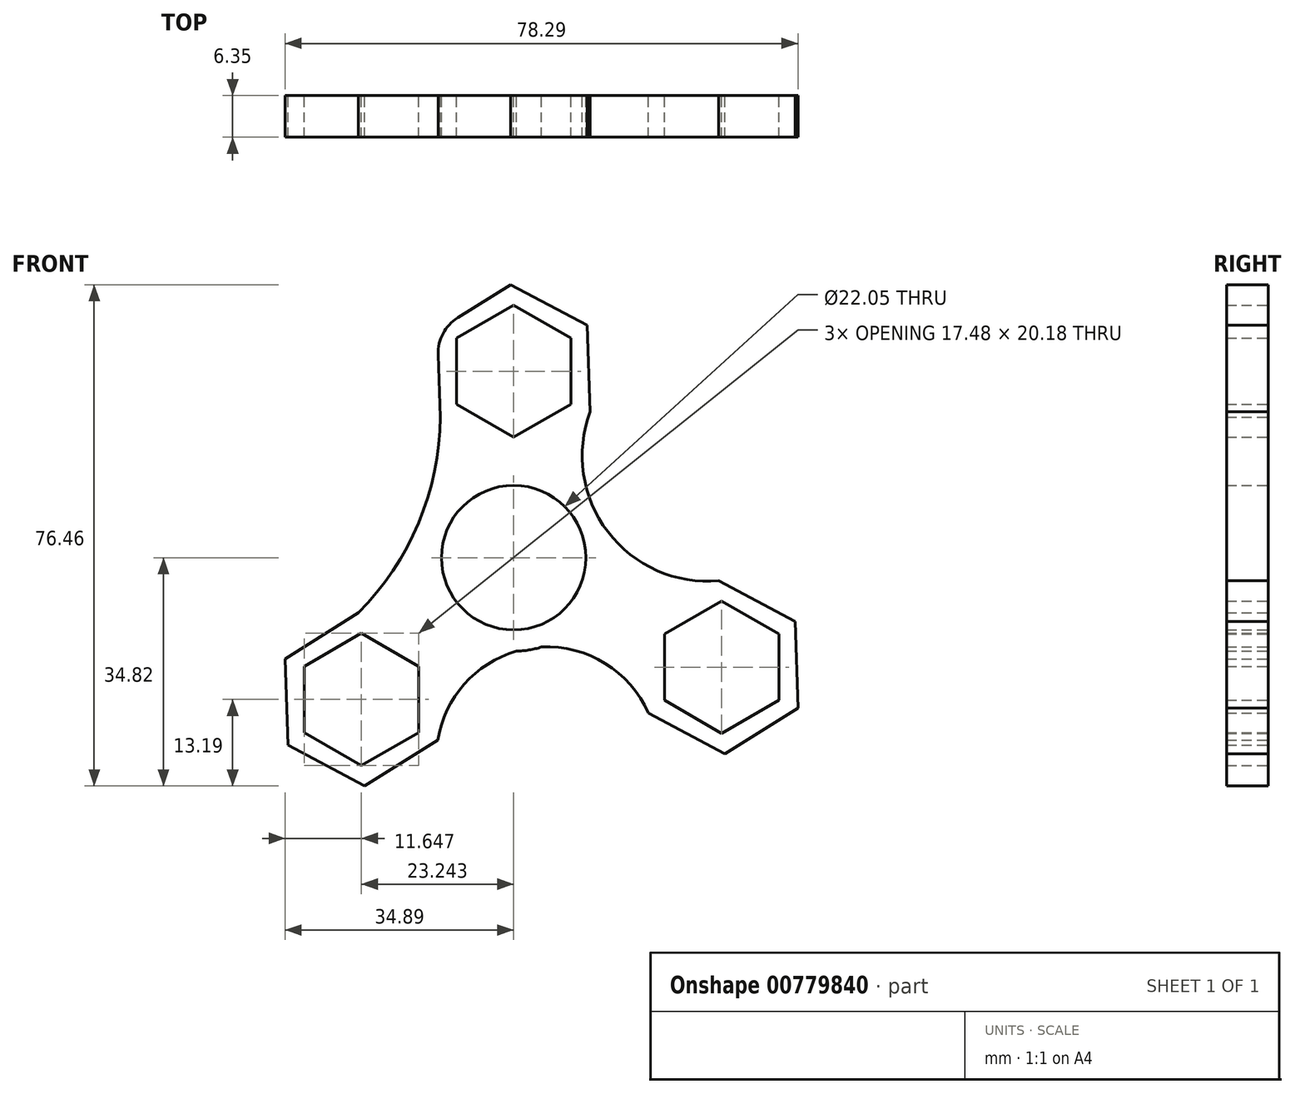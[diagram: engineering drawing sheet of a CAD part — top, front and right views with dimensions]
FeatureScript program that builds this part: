
annotation { "Feature Type Name" : "Feature", "Feature Type Description" : "" }
export const myFeature = defineFeature(function(context is Context, id is Id, definition is map)
    precondition{}
    {
        {
            var Q0;
            Q0=qCreatedBy(makeId("Front.planeOp"),FACE);
            var sketch = newSketch(context, id + "F0", { "sketchPlane" : qUnion([Q0])});
            skCircle(sketch, "E0", {"center": v(0, 0) * mm, "radius": 11.02 * mm});
            skCircle(sketch, "E1", {"center": v(0, 0) * mm, "radius": 14.29 * mm});
            skCircle(sketch, "E2.cCircle", {"center": v(0, 28.45) * mm, "radius": 8.74 * mm, "construction": true});
            skLineSegment(sketch, "E2.0", {"start": v(8.74, 33.5) * mm, "end": v(8.74, 23.4) * mm});
            skLineSegment(sketch, "E2.1", {"start": v(8.74, 23.4) * mm, "end": v(0, 18.36) * mm});
            skLineSegment(sketch, "E2.2", {"start": v(0, 18.36) * mm, "end": v(-8.74, 23.4) * mm});
            skLineSegment(sketch, "E2.3", {"start": v(-8.74, 23.4) * mm, "end": v(-8.74, 33.5) * mm});
            skLineSegment(sketch, "E2.4", {"start": v(-8.74, 33.5) * mm, "end": v(0, 38.54) * mm});
            skLineSegment(sketch, "E2.5", {"start": v(0, 38.54) * mm, "end": v(8.74, 33.5) * mm});
            skPoint(sketch, "E2.0.midPoint", {"position": v(8.74, 28.45) * mm});
            skCircle(sketch, "E3.cCircle", {"center": v(0, 28.45) * mm, "radius": 11.43 * mm, "construction": true});
            skLineSegment(sketch, "E3.0", {"start": v(-0.45, 41.64) * mm, "end": v(11.2, 35.44) * mm});
            skLineSegment(sketch, "E3.1", {"start": v(11.2, 35.44) * mm, "end": v(11.65, 22.25) * mm});
            skLineSegment(sketch, "E3.2", {"start": v(11.65, 22.25) * mm, "end": v(0.45, 15.26) * mm});
            skLineSegment(sketch, "E3.3", {"start": v(0.45, 15.26) * mm, "end": v(-11.2, 21.46) * mm});
            skLineSegment(sketch, "E3.4", {"start": v(-11.2, 21.46) * mm, "end": v(-11.52, 30.99) * mm});
            skLineSegment(sketch, "E3.5", {"start": v(-8.54, 36.6) * mm, "end": v(-0.45, 41.64) * mm});
            skPoint(sketch, "E3.0.midPoint", {"position": v(5.37, 38.54) * mm});
            skLineSegment(sketch, "E4.1.0", {"start": v(-23.24, -31.72) * mm, "end": v(-31.98, -26.67) * mm});
            skLineSegment(sketch, "E4.1.1", {"start": v(-31.98, -26.67) * mm, "end": v(-31.98, -16.59) * mm});
            skLineSegment(sketch, "E4.1.2", {"start": v(-31.98, -16.59) * mm, "end": v(-23.24, -11.54) * mm});
            skLineSegment(sketch, "E4.1.3", {"start": v(-23.24, -11.54) * mm, "end": v(-14.5, -16.59) * mm});
            skCircle(sketch, "E4.1.4", {"center": v(-23.24, -21.63) * mm, "radius": 8.74 * mm, "construction": true});
            skLineSegment(sketch, "E4.1.5", {"start": v(-14.5, -26.67) * mm, "end": v(-23.24, -31.72) * mm});
            skLineSegment(sketch, "E4.1.6", {"start": v(-14.5, -16.59) * mm, "end": v(-14.5, -26.67) * mm});
            skCircle(sketch, "E4.1.7", {"center": v(-23.24, -21.63) * mm, "radius": 11.43 * mm, "construction": true});
            skLineSegment(sketch, "E4.1.8", {"start": v(-11.6, -27.83) * mm, "end": v(-22.79, -34.82) * mm});
            skLineSegment(sketch, "E4.1.9", {"start": v(-12.05, -14.64) * mm, "end": v(-11.6, -27.83) * mm});
            skLineSegment(sketch, "E4.1.10", {"start": v(-23.7, -8.44) * mm, "end": v(-12.05, -14.64) * mm});
            skLineSegment(sketch, "E4.1.11", {"start": v(-34.9, -15.43) * mm, "end": v(-23.7, -8.44) * mm});
            skLineSegment(sketch, "E4.1.12", {"start": v(-34.44, -28.62) * mm, "end": v(-34.9, -15.43) * mm});
            skLineSegment(sketch, "E4.1.13", {"start": v(-22.79, -34.82) * mm, "end": v(-34.44, -28.62) * mm});
            skLineSegment(sketch, "E4.2.0", {"start": v(40.49, -11.67) * mm, "end": v(40.49, -21.76) * mm});
            skLineSegment(sketch, "E4.2.1", {"start": v(40.49, -21.76) * mm, "end": v(31.75, -26.8) * mm});
            skLineSegment(sketch, "E4.2.2", {"start": v(31.75, -26.8) * mm, "end": v(23.01, -21.76) * mm});
            skLineSegment(sketch, "E4.2.3", {"start": v(23.01, -21.76) * mm, "end": v(23.01, -11.67) * mm});
            skCircle(sketch, "E4.2.4", {"center": v(31.75, -16.72) * mm, "radius": 8.74 * mm, "construction": true});
            skLineSegment(sketch, "E4.2.5", {"start": v(31.75, -6.63) * mm, "end": v(40.49, -11.67) * mm});
            skLineSegment(sketch, "E4.2.6", {"start": v(23.01, -11.67) * mm, "end": v(31.75, -6.63) * mm});
            skCircle(sketch, "E4.2.7", {"center": v(31.75, -16.72) * mm, "radius": 11.43 * mm, "construction": true});
            skLineSegment(sketch, "E4.2.8", {"start": v(31.3, -3.53) * mm, "end": v(42.95, -9.73) * mm});
            skLineSegment(sketch, "E4.2.9", {"start": v(20.1, -10.52) * mm, "end": v(31.3, -3.53) * mm});
            skLineSegment(sketch, "E4.2.10", {"start": v(20.55, -23.7) * mm, "end": v(20.1, -10.52) * mm});
            skLineSegment(sketch, "E4.2.11", {"start": v(32.2, -29.9) * mm, "end": v(20.55, -23.7) * mm});
            skLineSegment(sketch, "E4.2.12", {"start": v(43.4, -22.92) * mm, "end": v(32.2, -29.9) * mm});
            skLineSegment(sketch, "E4.2.13", {"start": v(42.95, -9.73) * mm, "end": v(43.4, -22.92) * mm});
            skPoint(sketch, "E4.center", {"position": v(2.84, -3.3) * mm});
            skPoint(sketch, "E5.visualSharp", {"position": v(-11.65, 34.65) * mm});
            skArc(sketch, "E5.filletArc", {"start": v(-8.54, 36.6) * mm, "mid": v(-10.78, 34.2) * mm, "end": v(-11.52, 30.99) * mm});
            skArc(sketch, "E6", {"start": v(-23.7, -8.44) * mm, "mid": v(-14.53, 5.3) * mm, "end": v(-11.2, 21.46) * mm});
            skArc(sketch, "E7", {"start": v(11.65, 22.25) * mm, "mid": v(14.37, 3.95) * mm, "end": v(31.3, -3.53) * mm});
            skArc(sketch, "E8", {"start": v(20.55, -23.7) * mm, "mid": v(2.94, -13.76) * mm, "end": v(-11.6, -27.83) * mm});
            skSolve(sketch);
        }
        {
            var Q0;
            Q0 = qSketchRegion(id + "F0", true);
            var Q1;
            Q1=makeQuery(id+"F0.imprint","IMPRINT",FACE,{"disambiguationData":[TD([[makeQuery(id+"F0.imprint","IMPRINT",EDGE,{"derivedFrom":sQuery(id+"F0.wireOp",EDGE,"E0")}),-1.0]])]});
            extrude(context, id + "F1", {"entities" : qUnion([Q0, Q1]), "depth" : 6.35 * mm, "offsetDistance" : 25.4 * mm});
        }
    });
